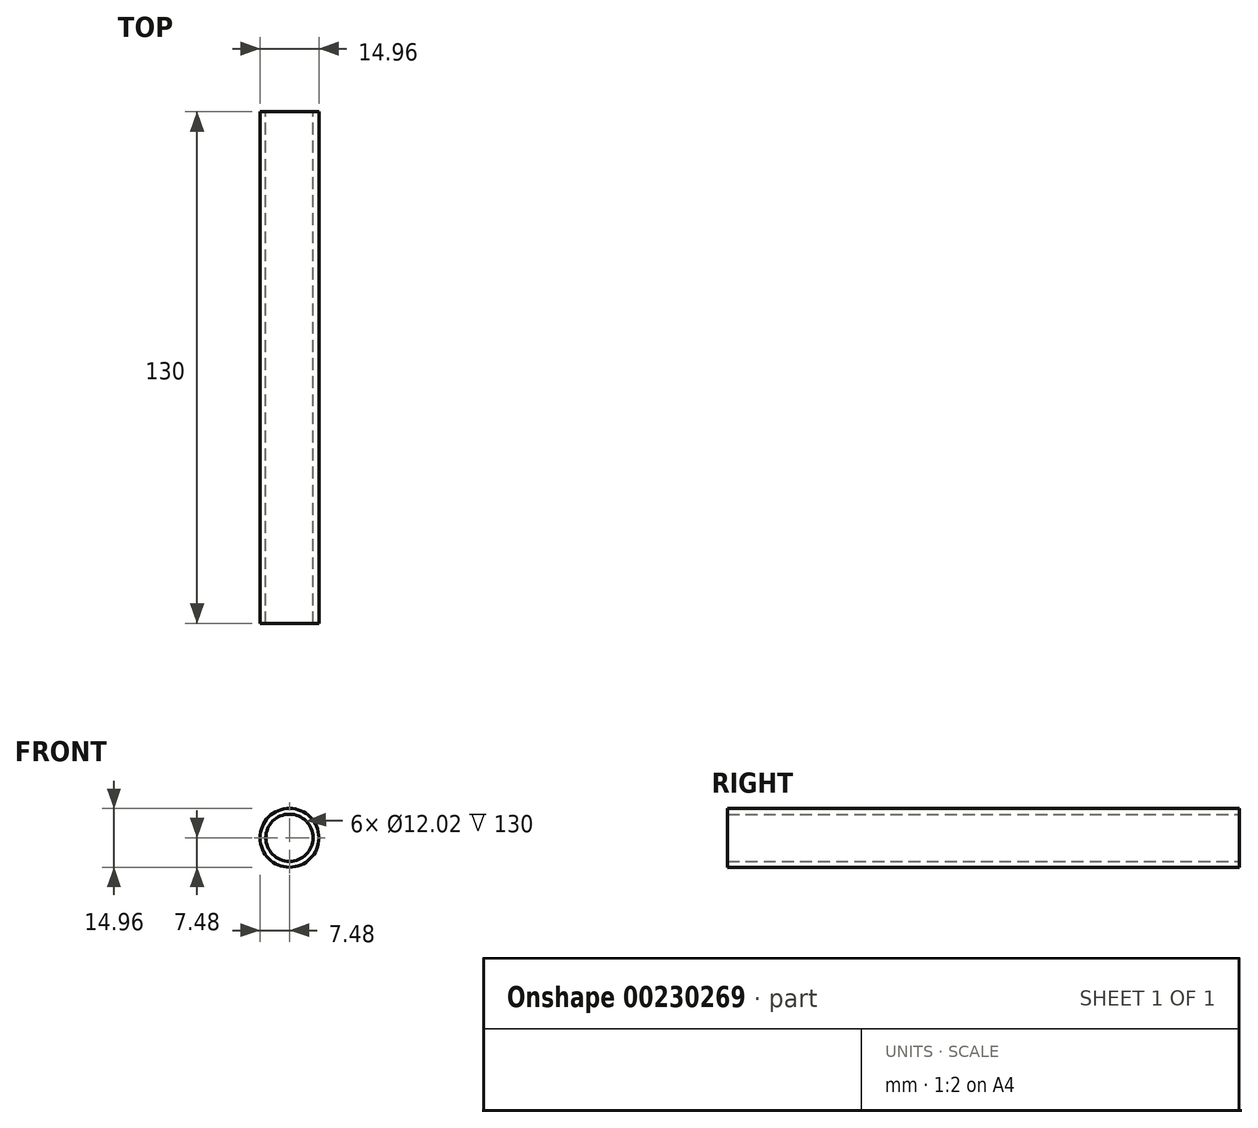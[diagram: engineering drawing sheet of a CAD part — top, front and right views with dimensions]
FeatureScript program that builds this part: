
annotation { "Feature Type Name" : "Feature", "Feature Type Description" : "" }
export const myFeature = defineFeature(function(context is Context, id is Id, definition is map)
    precondition{}
    {
        {
            var Q0;
            Q0=qCreatedBy(makeId("Front.planeOp"),FACE);
            var sketch = newSketch(context, id + "F0", { "sketchPlane" : qUnion([Q0])});
            skCircle(sketch, "E0", {"center": v(0, 0) * mm, "radius": 7.47 * mm});
            skCircle(sketch, "E1", {"center": v(0, 0) * mm, "radius": 6 * mm});
            skSolve(sketch);
        }
        {
            var Q0;
            Q0=makeQuery(id+"F0.imprint","IMPRINT",FACE,{"disambiguationData":[TD([[makeQuery(id+"F0.imprint","IMPRINT",EDGE,{"derivedFrom":sQuery(id+"F0.wireOp",EDGE,"E0")}),1.0]])]});
            extrude(context, id + "F1", {"entities" : qUnion([Q0]), "endBound" : BoundingType.SYMMETRIC, "depth" : 130 * mm});
        }
    });
